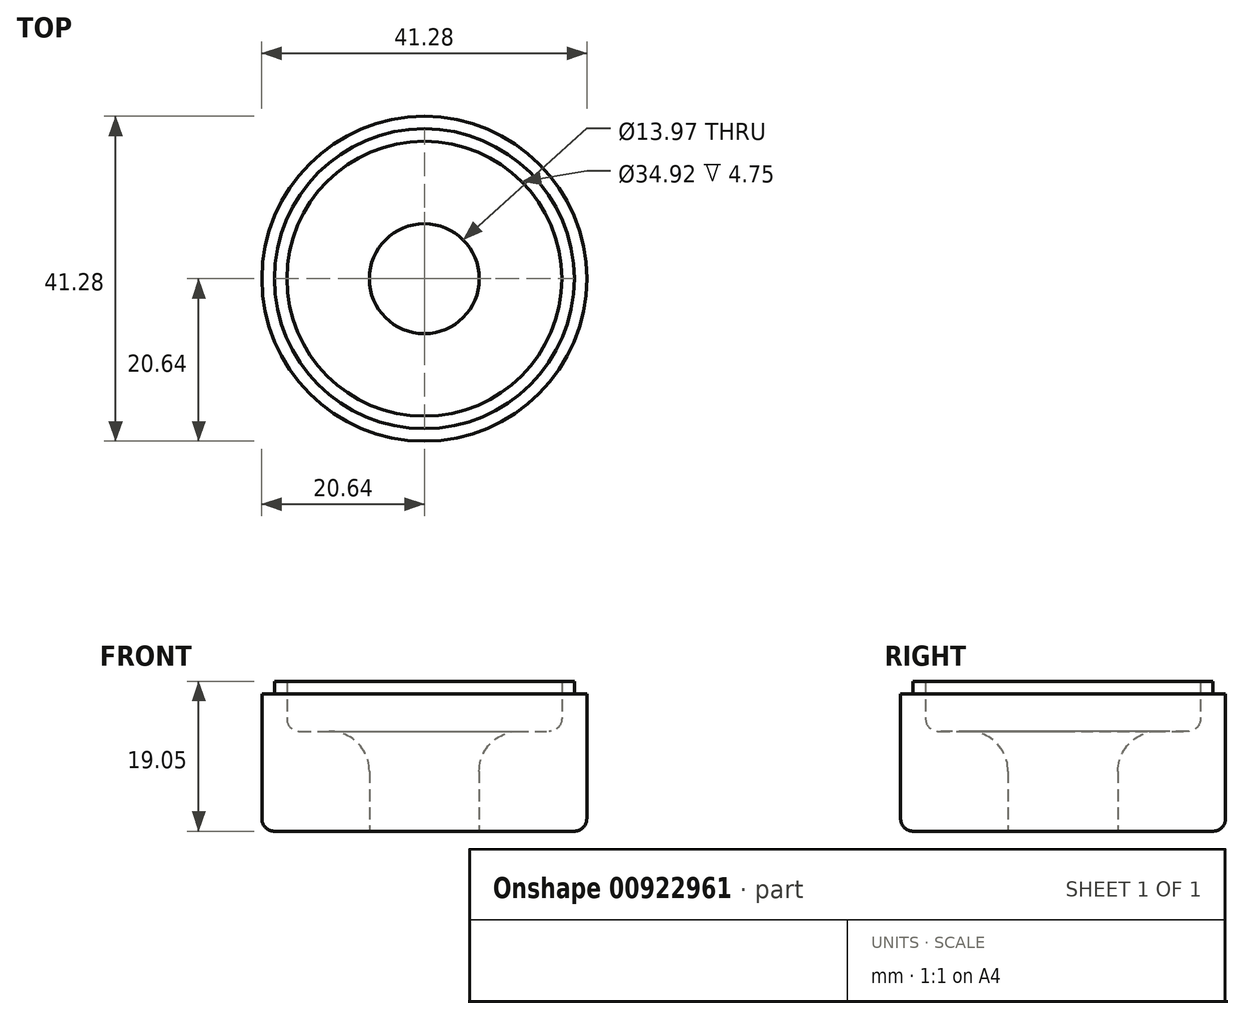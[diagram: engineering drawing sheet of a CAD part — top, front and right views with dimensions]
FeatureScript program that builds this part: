
annotation { "Feature Type Name" : "Feature", "Feature Type Description" : "" }
export const myFeature = defineFeature(function(context is Context, id is Id, definition is map)
    precondition{}
    {
        {
            var Q0;
            Q0=qCreatedBy(makeId("Front.planeOp"),FACE);
            var sketch = newSketch(context, id + "F0", { "sketchPlane" : qUnion([Q0])});
            skLineSegment(sketch, "E0", {"start": v(0, 0) * mm, "end": v(0, 35.76) * mm, "construction": true});
            skLineSegment(sketch, "E1", {"start": v(6.99, 0) * mm, "end": v(6.99, 12.7) * mm});
            skLineSegment(sketch, "E2", {"start": v(6.99, 12.7) * mm, "end": v(17.46, 12.7) * mm});
            skLineSegment(sketch, "E3", {"start": v(17.46, 12.7) * mm, "end": v(17.46, 19.05) * mm});
            skLineSegment(sketch, "E4", {"start": v(17.46, 19.05) * mm, "end": v(19.05, 19.05) * mm});
            skLineSegment(sketch, "E5", {"start": v(19.05, 19.05) * mm, "end": v(19.05, 17.46) * mm});
            skLineSegment(sketch, "E6", {"start": v(19.05, 17.46) * mm, "end": v(20.64, 17.46) * mm});
            skLineSegment(sketch, "E7", {"start": v(20.64, 17.46) * mm, "end": v(20.64, 0) * mm});
            skLineSegment(sketch, "E8", {"start": v(20.64, 0) * mm, "end": v(6.99, 0) * mm});
            skSolve(sketch);
        }
        {
            var Q0;
            Q0 = qSketchRegion(id + "F0", true);
            var Q1;
            Q1=sQuery(id+"F0.wireOp",EDGE,"E0");
            revolve(context, id + "F1", {"surfaceOperationType" : NewSurfaceOperationType.NEW, "entities" : qUnion([Q0]), "axis" : qUnion([Q1]), "revolveType" : RevolveType.FULL});
        }
        {
            var Q0;
            Q0=makeQuery(id+"F1.opRevolve","SWEPT_EDGE",EDGE,{"disambiguationData":[OSD([sQuery(id+"F0.wireOp",EDGE,"E2"),sQuery(id+"F0.wireOp",EDGE,"E3")])]});
            var Q1;
            Q1=makeQuery(id+"F1.opRevolve","SWEPT_EDGE",EDGE,{"disambiguationData":[OSD([sQuery(id+"F0.wireOp",EDGE,"E7"),sQuery(id+"F0.wireOp",EDGE,"E8")])]});
            fillet(context, id + "F2", {"entities" : qUnion([Q0, Q1]), "radius" : 1.6 * mm, "tangentPropagation" : true, "allowEdgeOverflow" : false});
        }
        {
            var Q0;
            Q0=makeQuery(id+"F1.opRevolve","SWEPT_EDGE",EDGE,{"disambiguationData":[OSD([sQuery(id+"F0.wireOp",EDGE,"E1"),sQuery(id+"F0.wireOp",EDGE,"E2")])]});
            fillet(context, id + "F3", {"entities" : qUnion([Q0]), "radius" : 5.08 * mm, "tangentPropagation" : true, "allowEdgeOverflow" : false});
        }
    });
